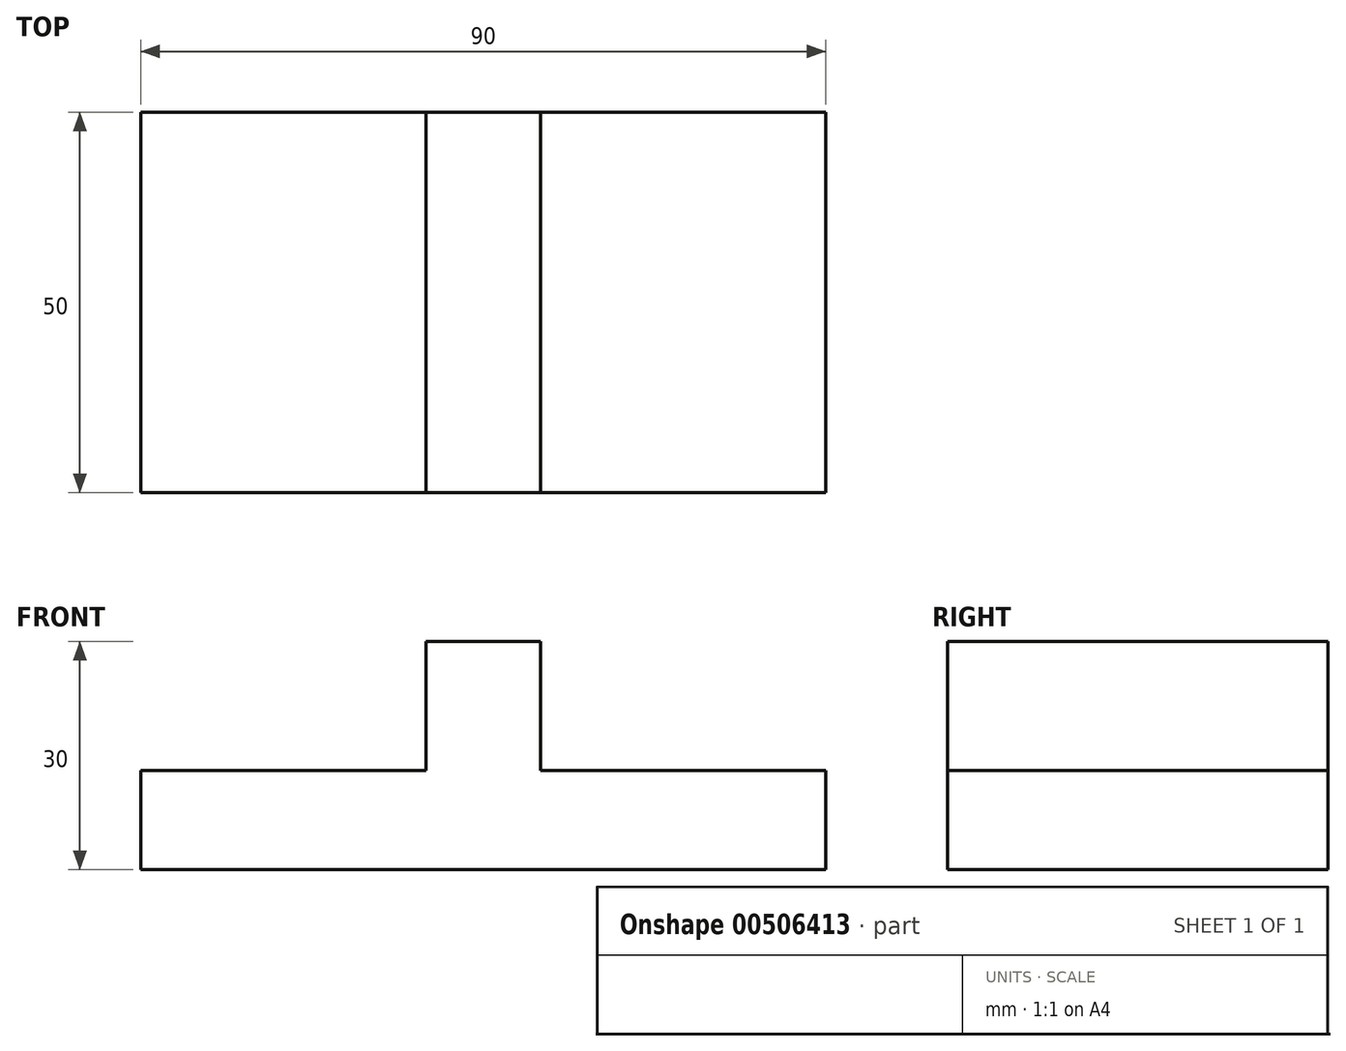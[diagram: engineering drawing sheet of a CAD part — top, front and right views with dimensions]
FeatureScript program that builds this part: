
annotation { "Feature Type Name" : "Feature", "Feature Type Description" : "" }
export const myFeature = defineFeature(function(context is Context, id is Id, definition is map)
    precondition{}
    {
        {
            var Q0;
            Q0=qCreatedBy(makeId("Front.planeOp"),FACE);
            var sketch = newSketch(context, id + "F0", { "sketchPlane" : qUnion([Q0])});
            skLineSegment(sketch, "E0", {"start": v(-45, 0) * mm, "end": v(-45, 13) * mm});
            skLineSegment(sketch, "E1", {"start": v(-45, 13) * mm, "end": v(-7.5, 13) * mm});
            skLineSegment(sketch, "E2", {"start": v(-7.5, 13) * mm, "end": v(-7.5, 30) * mm});
            skLineSegment(sketch, "E3", {"start": v(-7.5, 30) * mm, "end": v(7.5, 30) * mm});
            skLineSegment(sketch, "E4", {"start": v(7.5, 30) * mm, "end": v(7.5, 13) * mm});
            skLineSegment(sketch, "E5", {"start": v(7.5, 13) * mm, "end": v(45, 13) * mm});
            skLineSegment(sketch, "E6", {"start": v(45, 13) * mm, "end": v(45, 0) * mm});
            skLineSegment(sketch, "E7", {"start": v(45, 0) * mm, "end": v(-45, 0) * mm});
            skSolve(sketch);
        }
        {
            var Q0;
            Q0=makeQuery(id+"F0.imprint","IMPRINT",FACE,{"disambiguationData":[TD([[makeQuery(id+"F0.imprint","IMPRINT",EDGE,{"derivedFrom":sQuery(id+"F0.wireOp",EDGE,"E0")}),-1.0]])]});
            extrude(context, id + "F1", {"entities" : qUnion([Q0]), "depth" : 50 * mm});
        }
    });
